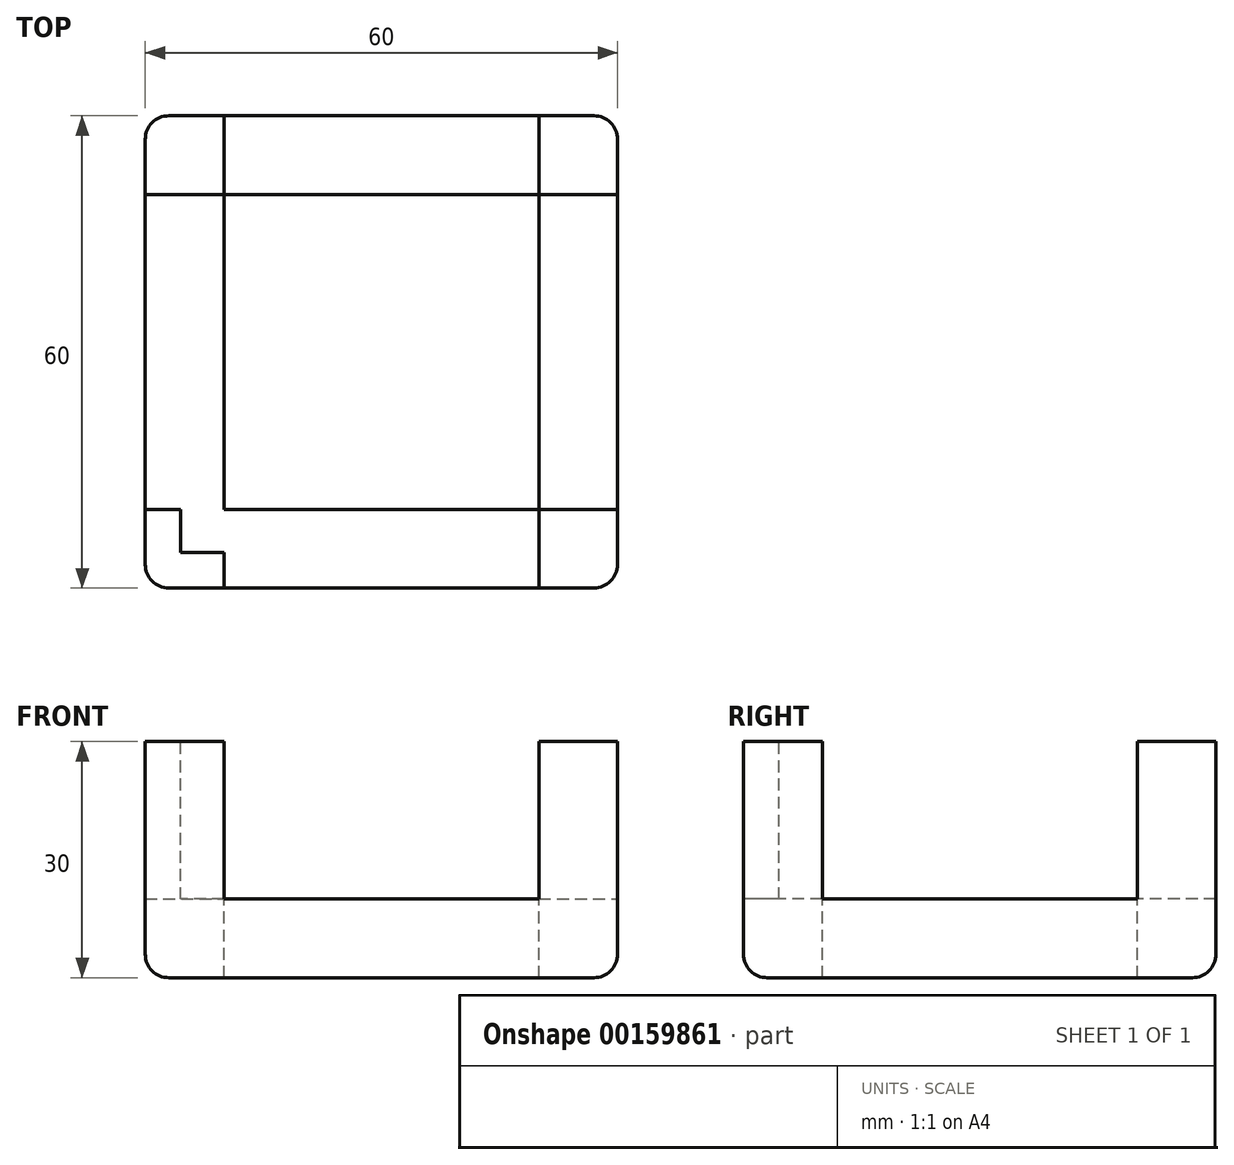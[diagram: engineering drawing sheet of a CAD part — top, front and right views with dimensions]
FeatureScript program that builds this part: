
annotation { "Feature Type Name" : "Feature", "Feature Type Description" : "" }
export const myFeature = defineFeature(function(context is Context, id is Id, definition is map)
    precondition{}
    {
        {
            var Q0;
            Q0=qCreatedBy(makeId("Top.planeOp"),FACE);
            var sketch = newSketch(context, id + "F0", { "sketchPlane" : qUnion([Q0])});
            skLineSegment(sketch, "E0.bottom", {"start": v(30, 30) * mm, "end": v(-30, 30) * mm});
            skLineSegment(sketch, "E0.top", {"start": v(30, -30) * mm, "end": v(-30, -30) * mm});
            skLineSegment(sketch, "E0.left", {"start": v(30, 30) * mm, "end": v(30, -30) * mm});
            skLineSegment(sketch, "E0.right", {"start": v(-30, 30) * mm, "end": v(-30, -30) * mm});
            skPoint(sketch, "E0.middle", {"position": v(0, 0) * mm});
            skSolve(sketch);
        }
        {
            var Q0;
            Q0=makeQuery(id+"F0.imprint","IMPRINT",FACE,{"disambiguationData":[TD([[makeQuery(id+"F0.imprint","IMPRINT",EDGE,{"derivedFrom":sQuery(id+"F0.wireOp",EDGE,"E0.bottom")}),1.0]])]});
            extrude(context, id + "F1", {"entities" : qUnion([Q0]), "depth" : 30 * mm});
        }
        {
            var Q0;
            Q0=makeQuery(id+"F1.opExtrude","CAP_FACE",FACE,{"disambiguationData":[OSD([sQuery(id+"F0.wireOp",EDGE,"E0.bottom"),sQuery(id+"F0.wireOp",EDGE,"E0.top"),sQuery(id+"F0.wireOp",EDGE,"E0.left"),sQuery(id+"F0.wireOp",EDGE,"E0.right")])],"isStart":false});
            var sketch = newSketch(context, id + "F2", { "sketchPlane" : qUnion([Q0])});
            skLineSegment(sketch, "E1.0", {"start": v(20, -20) * mm, "end": v(20, 20) * mm});
            skLineSegment(sketch, "E1.1", {"start": v(-20, -20) * mm, "end": v(20, -20) * mm});
            skLineSegment(sketch, "E1.2", {"start": v(-20, 20) * mm, "end": v(-20, -20) * mm});
            skLineSegment(sketch, "E1.3", {"start": v(20, 20) * mm, "end": v(-20, 20) * mm});
            skSolve(sketch);
        }
        {
            var Q0;
            Q0=makeQuery(id+"F2.imprint","IMPRINT",FACE,{"disambiguationData":[TD([[makeQuery(id+"F2.imprint","IMPRINT",EDGE,{"derivedFrom":sQuery(id+"F2.wireOp",EDGE,"E1.0")}),1.0]])]});
            extrude(context, id + "F3", {"entities" : qUnion([Q0]), "operationType" : NewBodyOperationType.REMOVE, "oppositeDirection" : true, "depth" : 30 * mm});
        }
        {
            var Q0;
            Q0=makeQuery(id+"F1.opExtrude","SWEPT_FACE",FACE,{"disambiguationData":[OSD([sQuery(id+"F0.wireOp",EDGE,"E0.left")])]});
            var sketch = newSketch(context, id + "F4", { "sketchPlane" : qUnion([Q0])});
            skLineSegment(sketch, "E2.0", {"start": v(20, 30) * mm, "end": v(20, 10) * mm});
            skLineSegment(sketch, "E2.1", {"start": v(20, 10) * mm, "end": v(-20, 10) * mm});
            skLineSegment(sketch, "E2.2", {"start": v(-20, 30) * mm, "end": v(-20, 10) * mm});
            skSolve(sketch);
        }
        {
            var Q0;
            {var subQ0=sQuery(id+"F4.wireOp",EDGE,"E2.0");Q0=makeQuery(id+"F4.imprint","IMPRINT",FACE,{"disambiguationData":[TD([[makeQuery(id+"F4.imprint","IMPRINT",EDGE,{"derivedFrom":subQ0}),-1.0]])]});}
            extrude(context, id + "F5", {"entities" : qUnion([Q0]), "operationType" : NewBodyOperationType.REMOVE, "oppositeDirection" : true, "depth" : 60 * mm});
        }
        {
            var Q0;
            Q0=makeQuery(id+"F1.opExtrude","SWEPT_FACE",FACE,{"disambiguationData":[OSD([sQuery(id+"F0.wireOp",EDGE,"E0.top")])]});
            var sketch = newSketch(context, id + "F6", { "sketchPlane" : qUnion([Q0])});
            skLineSegment(sketch, "E3.0", {"start": v(20, 30) * mm, "end": v(20, 10) * mm});
            skLineSegment(sketch, "E3.1", {"start": v(20, 10) * mm, "end": v(-20, 10) * mm});
            skLineSegment(sketch, "E3.2", {"start": v(-20, 30) * mm, "end": v(-20, 10) * mm});
            skSolve(sketch);
        }
        {
            var Q0;
            {var subQ0=sQuery(id+"F6.wireOp",EDGE,"E3.0");Q0=makeQuery(id+"F6.imprint","IMPRINT",FACE,{"disambiguationData":[TD([[makeQuery(id+"F6.imprint","IMPRINT",EDGE,{"derivedFrom":subQ0}),-1.0]])]});}
            extrude(context, id + "F7", {"entities" : qUnion([Q0]), "operationType" : NewBodyOperationType.REMOVE, "oppositeDirection" : true, "depth" : 60 * mm});
        }
        {
            var Q0;
            {var subQ1=sQuery(id+"F0.wireOp",EDGE,"E0.right");var subQ2=makeQuery(id+"F1.opExtrude","SWEPT_FACE",FACE,{"disambiguationData":[OSD([subQ1])]});var subQ4=sQuery(id+"F0.wireOp",EDGE,"E0.top");var subQ5=makeQuery(id+"F1.opExtrude","SWEPT_FACE",FACE,{"disambiguationData":[OSD([subQ4])]});var subQ6=sQuery(id+"F0.wireOp",EDGE,"E0.left");Q0=makeQuery(id+"F7.boolean.opBoolean","SPLIT",FACE,{"disambiguationData":[TD([subQ2])],"derivedFrom":makeQuery(id+"F5.boolean.opBoolean","SPLIT",FACE,{"disambiguationData":[TD([subQ5])],"derivedFrom":makeQuery(id+"F1.opExtrude","CAP_FACE",FACE,{"disambiguationData":[OSD([sQuery(id+"F0.wireOp",EDGE,"E0.bottom"),subQ4,subQ6,subQ1])],"isStart":false})})});}
            var sketch = newSketch(context, id + "F8", { "sketchPlane" : qUnion([Q0])});
            skLineSegment(sketch, "E4.bottom", {"start": v(-20, -20) * mm, "end": v(-25.5, -20) * mm});
            skLineSegment(sketch, "E4.top", {"start": v(-20, -25.5) * mm, "end": v(-25.5, -25.5) * mm});
            skLineSegment(sketch, "E4.left", {"start": v(-20, -20) * mm, "end": v(-20, -25.5) * mm});
            skLineSegment(sketch, "E4.right", {"start": v(-25.5, -20) * mm, "end": v(-25.5, -25.5) * mm});
            skSolve(sketch);
        }
        {
            var Q0;
            Q0=makeQuery(id+"F8.imprint","IMPRINT",FACE,{"disambiguationData":[TD([[makeQuery(id+"F8.imprint","IMPRINT",EDGE,{"derivedFrom":sQuery(id+"F8.wireOp",EDGE,"E4.bottom")}),-1.0]])]});
            extrude(context, id + "F9", {"entities" : qUnion([Q0]), "operationType" : NewBodyOperationType.REMOVE, "oppositeDirection" : true, "depth" : 20 * mm});
        }
        {
            var Q0;
            Q0=makeQuery(id+"F1.opExtrude","SWEPT_EDGE",EDGE,{"disambiguationData":[OSD([sQuery(id+"F0.wireOp",EDGE,"E0.bottom"),sQuery(id+"F0.wireOp",EDGE,"E0.left")])]});
            var Q1;
            Q1=makeQuery(id+"F1.opExtrude","CAP_EDGE",EDGE,{"disambiguationData":[OSD([sQuery(id+"F0.wireOp",EDGE,"E0.bottom")])],"isStart":true});
            var Q2;
            Q2=makeQuery(id+"F1.opExtrude","SWEPT_EDGE",EDGE,{"disambiguationData":[OSD([sQuery(id+"F0.wireOp",EDGE,"E0.bottom"),sQuery(id+"F0.wireOp",EDGE,"E0.right")])]});
            var Q3;
            Q3=makeQuery(id+"F1.opExtrude","SWEPT_EDGE",EDGE,{"disambiguationData":[OSD([sQuery(id+"F0.wireOp",EDGE,"E0.top"),sQuery(id+"F0.wireOp",EDGE,"E0.left")])]});
            var Q4;
            Q4=makeQuery(id+"F1.opExtrude","SWEPT_EDGE",EDGE,{"disambiguationData":[OSD([sQuery(id+"F0.wireOp",EDGE,"E0.top"),sQuery(id+"F0.wireOp",EDGE,"E0.right")])]});
            var Q5;
            Q5=makeQuery(id+"F1.opExtrude","CAP_EDGE",EDGE,{"disambiguationData":[OSD([sQuery(id+"F0.wireOp",EDGE,"E0.top")])],"isStart":true});
            var Q6;
            Q6=makeQuery(id+"F1.opExtrude","CAP_EDGE",EDGE,{"disambiguationData":[OSD([sQuery(id+"F0.wireOp",EDGE,"E0.right")])],"isStart":true});
            var Q7;
            Q7=makeQuery(id+"F1.opExtrude","CAP_EDGE",EDGE,{"disambiguationData":[OSD([sQuery(id+"F0.wireOp",EDGE,"E0.left")])],"isStart":true});
            fillet(context, id + "F10", {"entities" : qUnion([Q0, Q1, Q2, Q3, Q4, Q5, Q6, Q7]), "radius" : 3 * mm, "tangentPropagation" : true, "allowEdgeOverflow" : false});
        }
    });
